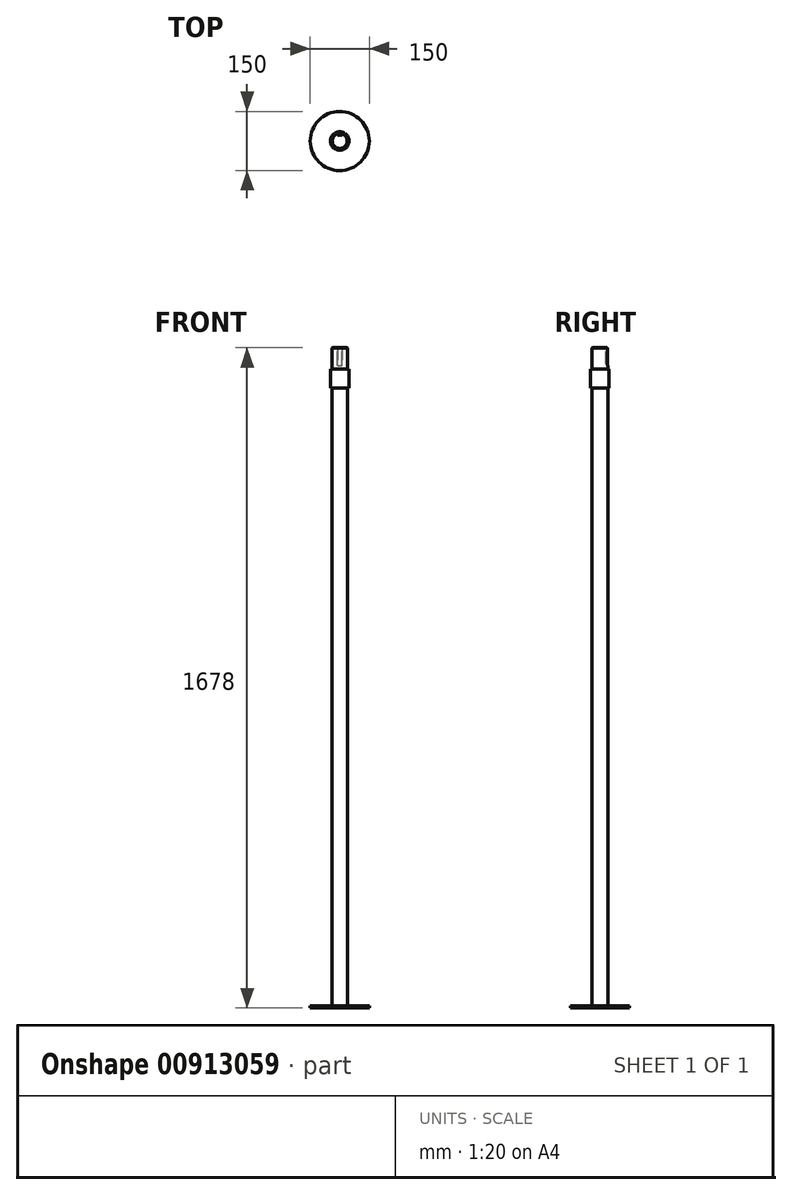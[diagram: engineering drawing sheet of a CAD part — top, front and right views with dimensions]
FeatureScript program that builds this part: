
annotation { "Feature Type Name" : "Feature", "Feature Type Description" : "" }
export const myFeature = defineFeature(function(context is Context, id is Id, definition is map)
    precondition{}
    {
        {
            var Q0;
            Q0=qCreatedBy(makeId("Top.planeOp"),FACE);
            var sketch = newSketch(context, id + "F0", { "sketchPlane" : qUnion([Q0])});
            skCircle(sketch, "E0", {"center": v(0, 0) * mm, "radius": 20 * mm});
            skSolve(sketch);
        }
        {
            var Q0;
            Q0 = qSketchRegion(id + "F0", true);
            extrude(context, id + "F1", {"entities" : qUnion([Q0]), "depth" : 1672 * mm, "offsetDistance" : 25 * mm});
        }
        {
            var Q0;
            Q0=makeQuery(id+"F1.opExtrude","CAP_FACE",FACE,{"disambiguationData":[OSD([sQuery(id+"F0.wireOp",EDGE,"E0")])],"isStart":true});
            var sketch = newSketch(context, id + "F2", { "sketchPlane" : qUnion([Q0])});
            skLineSegment(sketch, "E1", {"start": v(0, 0) * mm, "end": v(50, 0) * mm, "construction": true});
            skCircle(sketch, "E2", {"center": v(35.36, 35.36) * mm, "radius": 4.76 * mm, "construction": true});
            skLineSegment(sketch, "E3.1.0", {"start": v(0, 0) * mm, "end": v(0, 40) * mm, "construction": true});
            skCircle(sketch, "E3.1.1", {"center": v(-35.36, 35.36) * mm, "radius": 4.76 * mm, "construction": true});
            skLineSegment(sketch, "E3.2.0", {"start": v(0, 0) * mm, "end": v(-40, 0) * mm, "construction": true});
            skCircle(sketch, "E3.2.1", {"center": v(-35.36, -35.36) * mm, "radius": 4.76 * mm, "construction": true});
            skLineSegment(sketch, "E3.3.0", {"start": v(0, 0) * mm, "end": v(0, -40) * mm, "construction": true});
            skCircle(sketch, "E3.3.1", {"center": v(35.36, -35.36) * mm, "radius": 4.76 * mm, "construction": true});
            skPoint(sketch, "E3.center", {"position": v(0, 0) * mm});
            skCircle(sketch, "E4", {"center": v(0, 0) * mm, "radius": 75 * mm});
            skSolve(sketch);
        }
        {
            var Q0;
            Q0 = qSketchRegion(id + "F2", true);
            extrude(context, id + "F3", {"entities" : qUnion([Q0]), "operationType" : NewBodyOperationType.ADD, "depth" : 6 * mm, "offsetDistance" : 25 * mm});
        }
        {
            var Q0;
            Q0=makeQuery(id+"F3.opExtrude","CAP_FACE",FACE,{"disambiguationData":[OSD([sQuery(id+"F2.wireOp",EDGE,"E4")])],"isStart":true});
            cPlane(context, id + "F4", {"entities" : qUnion([Q0]), "cplaneType" : CPlaneType.OFFSET, "offset" : 1569.9 * mm, "width" : 150 * mm, "height" : 150 * mm});
        }
        {
            var Q0;
            Q0=qCreatedBy(id+"F4.planeOp",FACE);
            var sketch = newSketch(context, id + "F5", { "sketchPlane" : qUnion([Q0])});
            skCircle(sketch, "E5.0", {"center": v(0, 0) * mm, "radius": 23.5 * mm});
            skSolve(sketch);
        }
        {
            var Q0;
            Q0 = qSketchRegion(id + "F5", true);
            extrude(context, id + "F6", {"entities" : qUnion([Q0]), "operationType" : NewBodyOperationType.ADD, "depth" : 48 * mm, "offsetDistance" : 25 * mm});
        }
        {
            var Q0;
            Q0=makeQuery(id+"F6.boolean.opBoolean","INTERSECT",EDGE,{"derivedFrom":[makeQuery(id+"F1.opExtrude","SWEPT_FACE",FACE,{"disambiguationData":[OSD([sQuery(id+"F0.wireOp",EDGE,"E0")])]}),makeQuery(id+"F6.opExtrude","CAP_FACE",FACE,{"disambiguationData":[OSD([sQuery(id+"F5.wireOp",EDGE,"E5.0")])],"isStart":false})]});
            fillet(context, id + "F7", {"entities" : qUnion([Q0]), "radius" : 0.5 * mm, "tangentPropagation" : true, "allowEdgeOverflow" : false});
        }
        {
            var Q0;
            Q0=makeQuery(id+"F6.boolean.opBoolean","INTERSECT",EDGE,{"derivedFrom":[makeQuery(id+"F1.opExtrude","SWEPT_FACE",FACE,{"disambiguationData":[OSD([sQuery(id+"F0.wireOp",EDGE,"E0")])]}),makeQuery(id+"F6.opExtrude","CAP_FACE",FACE,{"disambiguationData":[OSD([sQuery(id+"F5.wireOp",EDGE,"E5.0")])],"isStart":true})]});
            fillet(context, id + "F8", {"entities" : qUnion([Q0]), "radius" : 1 * mm, "tangentPropagation" : true, "allowEdgeOverflow" : false});
        }
        {
            var Q0;
            Q0=makeQuery(id+"F1.opExtrude","CAP_FACE",FACE,{"disambiguationData":[OSD([sQuery(id+"F0.wireOp",EDGE,"E0")])],"isStart":false});
            var sketch = newSketch(context, id + "F9", { "sketchPlane" : qUnion([Q0])});
            skLineSegment(sketch, "E6", {"start": v(0, 20) * mm, "end": v(0, 15) * mm, "construction": true});
            skLineSegment(sketch, "E7", {"start": v(-6, 20) * mm, "end": v(6, 20) * mm});
            skLineSegment(sketch, "E8", {"start": v(-6, 15) * mm, "end": v(6, 15) * mm});
            skLineSegment(sketch, "E9", {"start": v(-6, 20) * mm, "end": v(-6, 15) * mm});
            skLineSegment(sketch, "E10", {"start": v(6, 20) * mm, "end": v(6, 15) * mm});
            skPoint(sketch, "E11.orphan", {"position": v(-7.97, 15) * mm});
            skPoint(sketch, "E12.orphan", {"position": v(-8.67, 20) * mm});
            skSolve(sketch);
        }
        {
            var Q0;
            Q0 = qSketchRegion(id + "F9", true);
            var Q1;
            Q1 = qConstructionFilter(qBodyType(qCreatedBy(id + "F9" ,EDGE), BodyType.WIRE), ConstructionObject.NO);
            extrude(context, id + "F10", {"entities" : qUnion([Q0]), "operationType" : NewBodyOperationType.REMOVE, "surfaceEntities" : qUnion([Q1]), "oppositeDirection" : true, "depth" : 45 * mm, "offsetDistance" : 25 * mm});
        }
        {
            var Q0;
            Q0=makeQuery(id+"F10.boolean.opBoolean","COPY",EDGE,{"derivedFrom":makeQuery(id+"F10.opExtrude","CAP_EDGE",EDGE,{"disambiguationData":[OSD([sQuery(id+"F9.wireOp",EDGE,"E8")])],"isStart":false})});
            fillet(context, id + "F11", {"entities" : qUnion([Q0]), "radius" : 5 * mm, "tangentPropagation" : true, "allowEdgeOverflow" : false});
        }
        {
            var Q0;
            Q0=makeQuery(id+"F1.opExtrude","CAP_EDGE",EDGE,{"disambiguationData":[OSD([sQuery(id+"F0.wireOp",EDGE,"E0")])],"isStart":false});
            chamfer(context, id + "F12", {"entities" : qUnion([Q0]), "chamferType" : ChamferType.OFFSET_ANGLE, "width" : 1 * mm, "oppositeDirection" : false, "angle" : 45 * degree, "tangentPropagation" : true});
        }
    });
